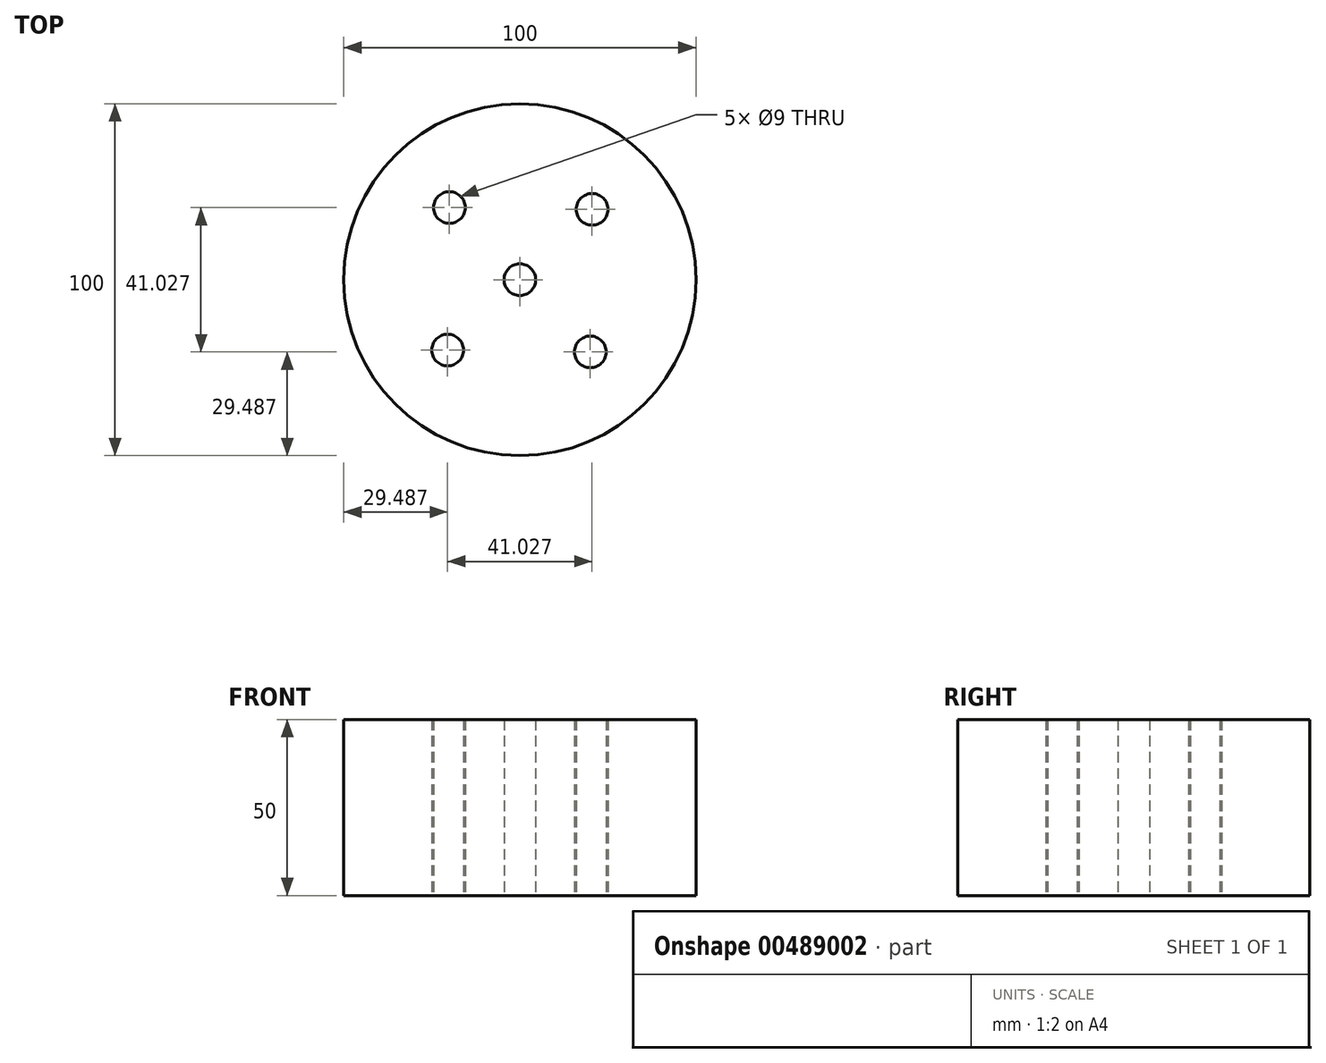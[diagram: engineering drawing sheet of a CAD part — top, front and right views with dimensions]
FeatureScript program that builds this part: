
annotation { "Feature Type Name" : "Feature", "Feature Type Description" : "" }
export const myFeature = defineFeature(function(context is Context, id is Id, definition is map)
    precondition{}
    {
        {
            var Q0;
            Q0=qCreatedBy(makeId("Top.planeOp"),FACE);
            var sketch = newSketch(context, id + "F0", { "sketchPlane" : qUnion([Q0])});
            skCircle(sketch, "E0", {"center": v(0, 0) * mm, "radius": 4.5 * mm});
            skCircle(sketch, "E1", {"center": v(0, 0) * mm, "radius": 50 * mm});
            skLineSegment(sketch, "E2", {"start": v(0.51, 0) * mm, "end": v(20.51, 0) * mm, "construction": true});
            skLineSegment(sketch, "E3", {"start": v(20.51, 20) * mm, "end": v(20.51, 0) * mm, "construction": true});
            skCircle(sketch, "E4", {"center": v(20.51, 20) * mm, "radius": 4.5 * mm});
            skCircle(sketch, "E5.1.0", {"center": v(-20, 20.51) * mm, "radius": 4.5 * mm});
            skCircle(sketch, "E5.2.0", {"center": v(-20.51, -20) * mm, "radius": 4.5 * mm});
            skCircle(sketch, "E5.3.0", {"center": v(20, -20.51) * mm, "radius": 4.5 * mm});
            skSolve(sketch);
        }
        {
            var Q0;
            Q0=makeQuery(id+"F0.imprint","IMPRINT",FACE,{"disambiguationData":[TD([[makeQuery(id+"F0.imprint","IMPRINT",EDGE,{"derivedFrom":sQuery(id+"F0.wireOp",EDGE,"E0")}),-1.0]])]});
            extrude(context, id + "F1", {"entities" : qUnion([Q0]), "depth" : 50 * mm});
        }
    });
